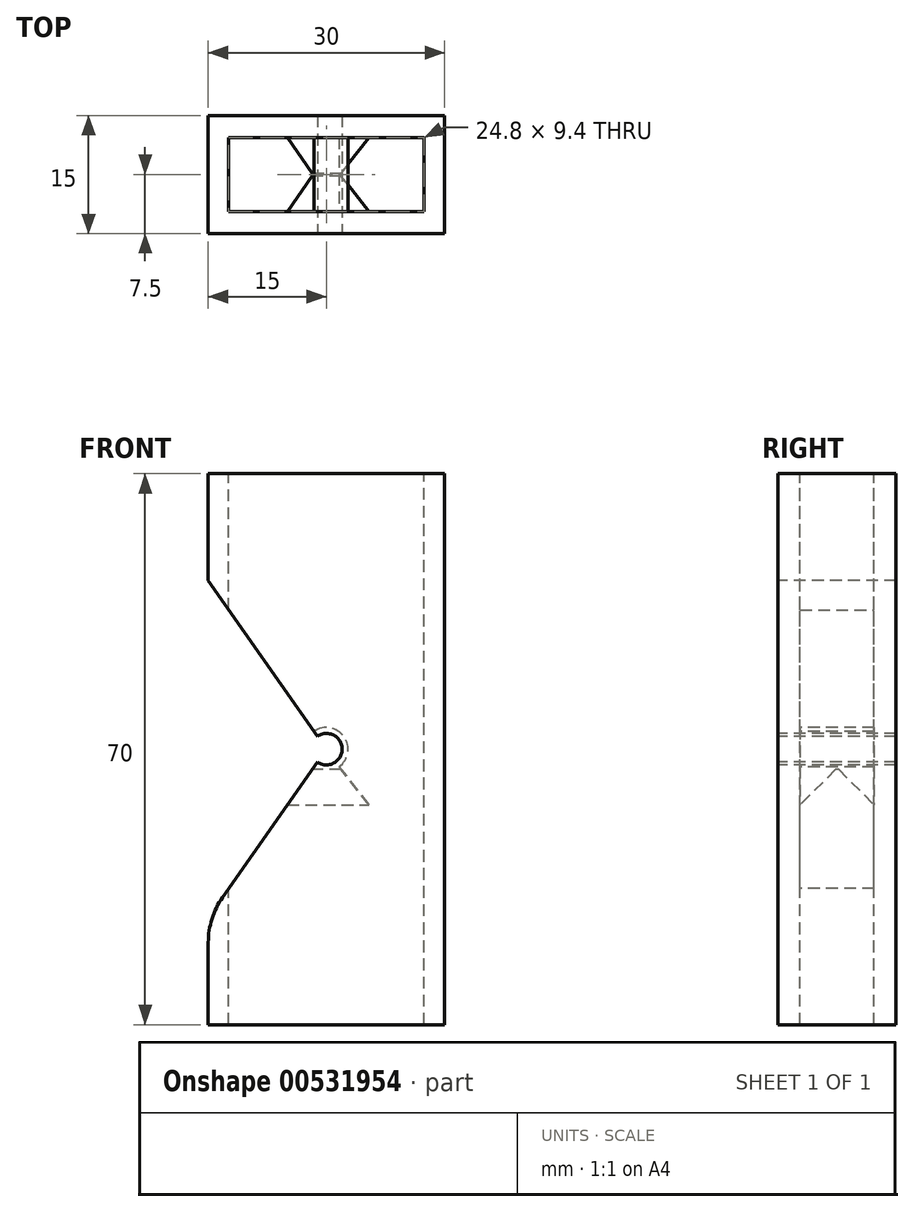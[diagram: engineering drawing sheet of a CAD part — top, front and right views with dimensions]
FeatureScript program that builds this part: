
annotation { "Feature Type Name" : "Feature", "Feature Type Description" : "" }
export const myFeature = defineFeature(function(context is Context, id is Id, definition is map)
    precondition{}
    {
        {
            var Q0;
            Q0=qCreatedBy(makeId("Front.planeOp"),FACE);
            var sketch = newSketch(context, id + "F0", { "sketchPlane" : qUnion([Q0])});
            skLineSegment(sketch, "E0.bottom", {"start": v(15, 35) * mm, "end": v(-15, 35) * mm});
            skLineSegment(sketch, "E0.top", {"start": v(15, -35) * mm, "end": v(-15, -35) * mm});
            skLineSegment(sketch, "E0.left", {"start": v(15, 35) * mm, "end": v(15, -35) * mm});
            skLineSegment(sketch, "E0.right", {"start": v(-15, 35) * mm, "end": v(-15, -35) * mm});
            skPoint(sketch, "E0.middle", {"position": v(0, 0) * mm});
            skSolve(sketch);
        }
        {
            var Q0;
            Q0=makeQuery(id+"F0.imprint","IMPRINT",FACE,{"disambiguationData":[TD([[makeQuery(id+"F0.imprint","IMPRINT",EDGE,{"derivedFrom":sQuery(id+"F0.wireOp",EDGE,"E0.bottom")}),1.0]])]});
            extrude(context, id + "F1", {"entities" : qUnion([Q0]), "depth" : 15 * mm, "offsetDistance" : 25 * mm});
        }
        {
            var Q0;
            Q0=makeQuery(id+"F1.opExtrude","SWEPT_FACE",FACE,{"disambiguationData":[OSD([sQuery(id+"F0.wireOp",EDGE,"E0.bottom")])]});
            var sketch = newSketch(context, id + "F2", { "sketchPlane" : qUnion([Q0])});
            skLineSegment(sketch, "E1.bottom", {"start": v(12.4, -12.2) * mm, "end": v(-12.4, -12.2) * mm});
            skLineSegment(sketch, "E1.top", {"start": v(12.4, -2.8) * mm, "end": v(-12.4, -2.8) * mm});
            skLineSegment(sketch, "E1.left", {"start": v(12.4, -12.2) * mm, "end": v(12.4, -2.8) * mm});
            skLineSegment(sketch, "E1.right", {"start": v(-12.4, -12.2) * mm, "end": v(-12.4, -2.8) * mm});
            skPoint(sketch, "E1.middle", {"position": v(0, -7.5) * mm});
            skPoint(sketch, "E1.middle.positionSnap0", {"position": v(-15, -7.5) * mm});
            skPoint(sketch, "E1.centerSnap0", {"position": v(-15, -7.5) * mm});
            skSolve(sketch);
        }
        {
            var Q0;
            Q0 = qSketchRegion(id + "F2", true);
            extrude(context, id + "F3", {"entities" : qUnion([Q0]), "operationType" : NewBodyOperationType.REMOVE, "endBound" : BoundingType.THROUGH_ALL, "oppositeDirection" : true, "depth" : 25 * mm, "offsetDistance" : 25 * mm});
        }
        {
            var Q0;
            Q0=makeQuery(id+"F1.opExtrude","CAP_FACE",FACE,{"disambiguationData":[OSD([sQuery(id+"F0.wireOp",EDGE,"E0.bottom"),sQuery(id+"F0.wireOp",EDGE,"E0.top"),sQuery(id+"F0.wireOp",EDGE,"E0.left"),sQuery(id+"F0.wireOp",EDGE,"E0.right")])],"isStart":false});
            var sketch = newSketch(context, id + "F4", { "sketchPlane" : qUnion([Q0])});
            skLineSegment(sketch, "E2", {"start": v(-15, 21.42) * mm, "end": v(-1.15, 1.64) * mm});
            skLineSegment(sketch, "E3", {"start": v(-1.15, -1.64) * mm, "end": v(-15, -21.42) * mm});
            skLineSegment(sketch, "E4", {"start": v(-15, -21.42) * mm, "end": v(-15, 21.42) * mm});
            skArc(sketch, "E5", {"start": v(-1.15, -1.64) * mm, "mid": v(2, 0) * mm, "end": v(-1.15, 1.64) * mm});
            skSolve(sketch);
        }
        {
            var Q0;
            Q0 = qSketchRegion(id + "F4", true);
            extrude(context, id + "F5", {"entities" : qUnion([Q0]), "operationType" : NewBodyOperationType.REMOVE, "endBound" : BoundingType.THROUGH_ALL, "oppositeDirection" : true, "depth" : 25 * mm, "offsetDistance" : 25 * mm});
        }
        {
            var Q0;
            Q0=makeQuery(id+"F1.opExtrude","CAP_FACE",FACE,{"disambiguationData":[OSD([sQuery(id+"F0.wireOp",EDGE,"E0.bottom"),sQuery(id+"F0.wireOp",EDGE,"E0.top"),sQuery(id+"F0.wireOp",EDGE,"E0.left"),sQuery(id+"F0.wireOp",EDGE,"E0.right")])],"isStart":false});
            var sketch = newSketch(context, id + "F6", { "sketchPlane" : qUnion([Q0])});
            skLineSegment(sketch, "E6", {"start": v(-1.15, -1.64) * mm, "end": v(-1.8, -2.58) * mm});
            skArc(sketch, "E7", {"start": v(1.6, -2.23) * mm, "mid": v(2.24, 1.6) * mm, "end": v(-1.58, 2.25) * mm});
            skLineSegment(sketch, "E8", {"start": v(-1.15, 1.64) * mm, "end": v(-1.58, 2.25) * mm});
            skArc(sketch, "E9", {"start": v(-1.15, -1.64) * mm, "mid": v(2, 0) * mm, "end": v(-1.15, 1.64) * mm});
            skLineSegment(sketch, "E10", {"start": v(1.88, -2.58) * mm, "end": v(-1.8, -2.58) * mm});
            skLineSegment(sketch, "E11", {"start": v(1.88, -2.58) * mm, "end": v(1.6, -2.23) * mm});
            skPoint(sketch, "E12.orphan", {"position": v(1.15, -1.64) * mm});
            skSolve(sketch);
        }
        {
            var Q0;
            Q0 = qSketchRegion(id + "F6", true);
            extrude(context, id + "F7", {"entities" : qUnion([Q0]), "operationType" : NewBodyOperationType.ADD, "oppositeDirection" : true, "depth" : 15 * mm, "offsetDistance" : 25 * mm});
        }
        {
            var Q0;
            Q0=makeQuery(id+"F7.boolean.opBoolean","INTERSECT",EDGE,{"derivedFrom":[makeQuery(id+"F3.boolean.opBoolean","COPY",FACE,{"derivedFrom":makeQuery(id+"F3.opExtrude","SWEPT_FACE",FACE,{"disambiguationData":[OSD([sQuery(id+"F2.wireOp",EDGE,"E1.top")])]})}),makeQuery(id+"F7.opExtrude","SWEPT_FACE",FACE,{"disambiguationData":[OSD([sQuery(id+"F6.wireOp",EDGE,"E10")])]})]});
            var Q1;
            Q1=makeQuery(id+"F7.boolean.opBoolean","INTERSECT",EDGE,{"derivedFrom":[makeQuery(id+"F3.boolean.opBoolean","COPY",FACE,{"derivedFrom":makeQuery(id+"F3.opExtrude","SWEPT_FACE",FACE,{"disambiguationData":[OSD([sQuery(id+"F2.wireOp",EDGE,"E1.bottom")])]})}),makeQuery(id+"F7.opExtrude","SWEPT_FACE",FACE,{"disambiguationData":[OSD([sQuery(id+"F6.wireOp",EDGE,"E10")])]})]});
            chamfer(context, id + "F8", {"entities" : qUnion([Q0, Q1]), "width" : 4.5 * mm, "tangentPropagation" : true});
        }
        {
            var Q0;
            Q0=makeQuery(id+"F5.boolean.opBoolean","COPY",EDGE,{"derivedFrom":makeQuery(id+"F5.opExtrude","SWEPT_EDGE",EDGE,{"disambiguationData":[OSD([sQuery(id+"F0.wireOp",EDGE,"E0.right"),sQuery(id+"F4.wireOp",EDGE,"E2"),sQuery(id+"F4.wireOp",EDGE,"E4")])]})});
            var Q1;
            Q1=makeQuery(id+"F5.boolean.opBoolean","COPY",EDGE,{"derivedFrom":makeQuery(id+"F5.opExtrude","SWEPT_EDGE",EDGE,{"disambiguationData":[OSD([sQuery(id+"F0.wireOp",EDGE,"E0.right"),sQuery(id+"F4.wireOp",EDGE,"E3"),sQuery(id+"F4.wireOp",EDGE,"E4")])]})});
            fillet(context, id + "F9", {"entities" : qUnion([Q0, Q1]), "radius" : 10 * mm, "tangentPropagation" : true, "allowEdgeOverflow" : false});
        }
    });
